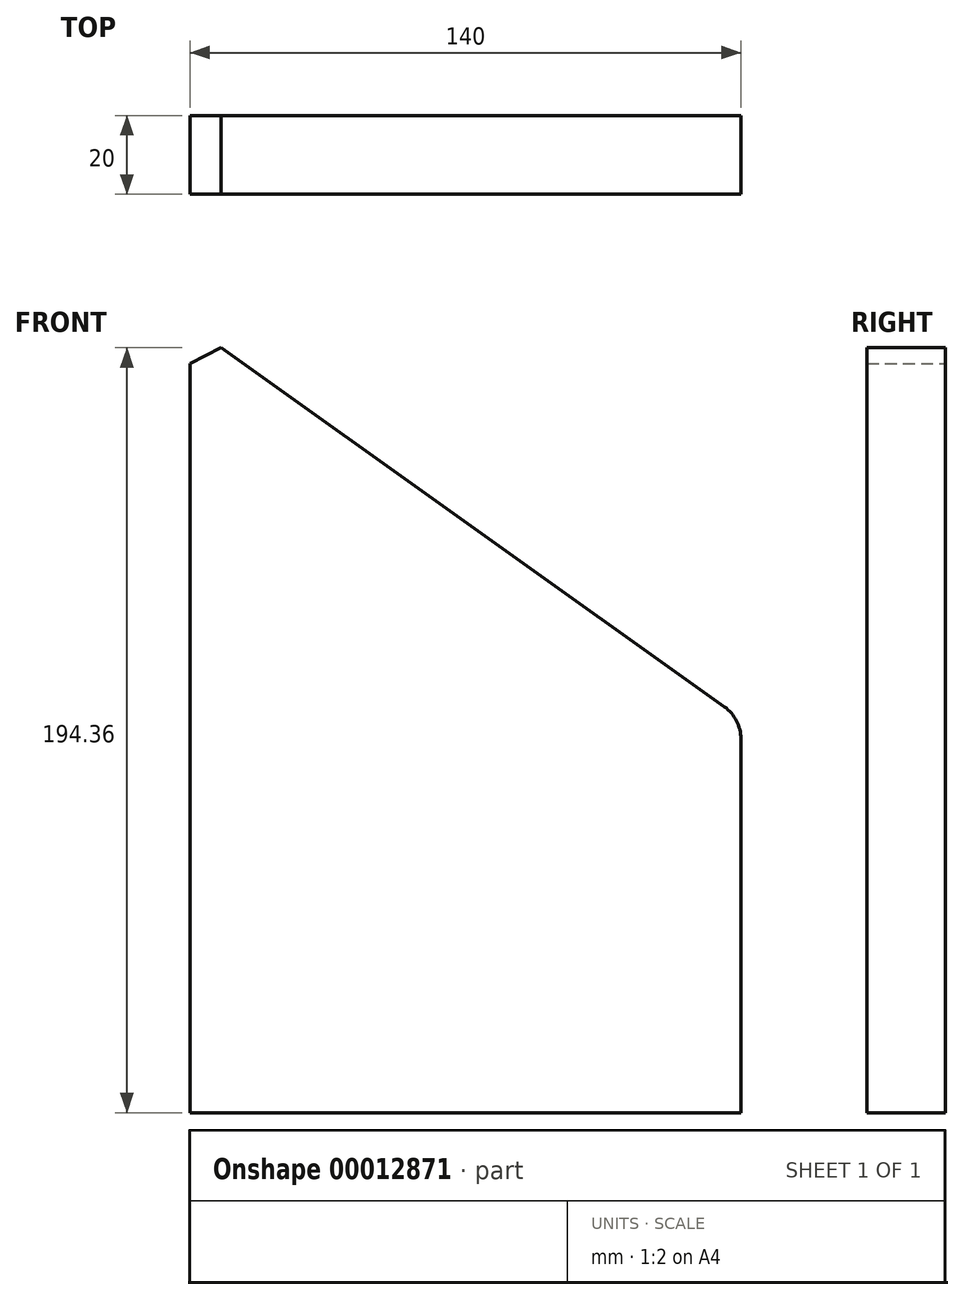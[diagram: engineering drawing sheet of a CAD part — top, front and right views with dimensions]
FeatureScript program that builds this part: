
annotation { "Feature Type Name" : "Feature", "Feature Type Description" : "" }
export const myFeature = defineFeature(function(context is Context, id is Id, definition is map)
    precondition{}
    {
        {
            var Q0;
            Q0=qCreatedBy(makeId("Front.planeOp"),FACE);
            var sketch = newSketch(context, id + "F0", { "sketchPlane" : qUnion([Q0])});
            skLineSegment(sketch, "E0", {"start": v(-140, 180.58) * mm, "end": v(-140, 0) * mm});
            skLineSegment(sketch, "E1", {"start": v(-140, 0) * mm, "end": v(0, 0) * mm});
            skLineSegment(sketch, "E2", {"start": v(0, 0) * mm, "end": v(0, 94.98) * mm});
            skLineSegment(sketch, "E3", {"start": v(-4.2, 103.12) * mm, "end": v(-124.2, 188.72) * mm});
            skPoint(sketch, "E4.visualSharp", {"position": v(-140, 200) * mm});
            skPoint(sketch, "E5.visualSharp", {"position": v(0, 100.13) * mm});
            skArc(sketch, "E5.filletArc", {"start": v(0, 94.98) * mm, "mid": v(-1.1, 99.56) * mm, "end": v(-4.2, 103.12) * mm});
            skLineSegment(sketch, "E6", {"start": v(-124.2, 188.72) * mm, "end": v(-140, 200) * mm});
            skLineSegment(sketch, "E7", {"start": v(-140, 180.58) * mm, "end": v(-140, 200) * mm});
            skSolve(sketch);
        }
        {
            var Q0;
            Q0=makeQuery(id+"F0.imprint","IMPRINT",FACE,{"disambiguationData":[TD([[makeQuery(id+"F0.imprint","IMPRINT",EDGE,{"derivedFrom":sQuery(id+"F0.wireOp",EDGE,"E0")}),1.0]])]});
            extrude(context, id + "F1", {"entities" : qUnion([Q0]), "endBound" : BoundingType.SYMMETRIC, "depth" : 20 * mm});
        }
        {
            var Q0;
            Q0=makeQuery(id+"F1.opExtrude","SWEPT_EDGE",EDGE,{"disambiguationData":[OSD([sQuery(id+"F0.wireOp",EDGE,"E6"),sQuery(id+"F0.wireOp",EDGE,"E7")])]});
            chamfer(context, id + "F2", {"entities" : qUnion([Q0]), "width" : 5 * mm, "tangentPropagation" : true});
        }
    });
